# Revit family: _VRD__Vicky_Ring_Downward_100W_3000K_BK
name_source: partatom
category: Lighting Fixtures
units: mm (PartAtom-declared; Revit-internal decimal feet)

## family parameters
Cut with Voids When Loaded = No
Host = Face
Light Source = Yes
Maintain Annotation Orientation = No
Part Type = Normal
Room Calculation Point = No
Round Connector Dimension = Use Diameter
Shared = No

## types (1)
- VRD-10059-30901-ACPMK-BK
    Apparent Load = 125 VA
    Average life based on 77F(HRS) = 50000
    B = 0' - 3 1/2"
    B1 = 2' - 5 11/32"
    B2 = 2' - 1 27/32"
    CRI = 90
    Canopy Height = 0' - 2"
    Color Filter = 16777215
    D1 = 0' - 5"
    D2 = 0' - 3 1/2"
    Default Elevation = 0' - 3 1/2"
    Description = The Vicky Ring light is a unique ring-style light with an LED light source illuminating downward
    Dimming / Control = 0-10V
    Dimming Lamp Color Temperature Shift = <None>
    Finish/Color = Aluminum
    Fixture Diameter = 4' - 11 3/32"
    Fixture Height = 4' - 0"
    Fixture Width = 0' - 0"
    H1 = 4' - 4 5/16"
    H2 = 3' - 9 15/32"
    IP Rating = 20
    Inner Diameter = 2' - 4 1/4"
    Inside Body = No
    Inside Body Material = <By Category>
    Load Classification = Lighting
    Manufacturer = Above All Lighting
    Model = VRD-10059-30901-ACPMK-BK
    Photometric Web File = VRD-10059-30901.ies
    Power Factor = 1
    Tilt Angle = -90.00°
    Type Comments = Vicky Ring Downward Light
    URL = https://www.abovealllighting.com
    Voltage = 120-277 V
    Wattage Comments = 100W

## geometry (parser evidence)
native form markers: Sweep x14
no freeform markers — native parametric forms only
